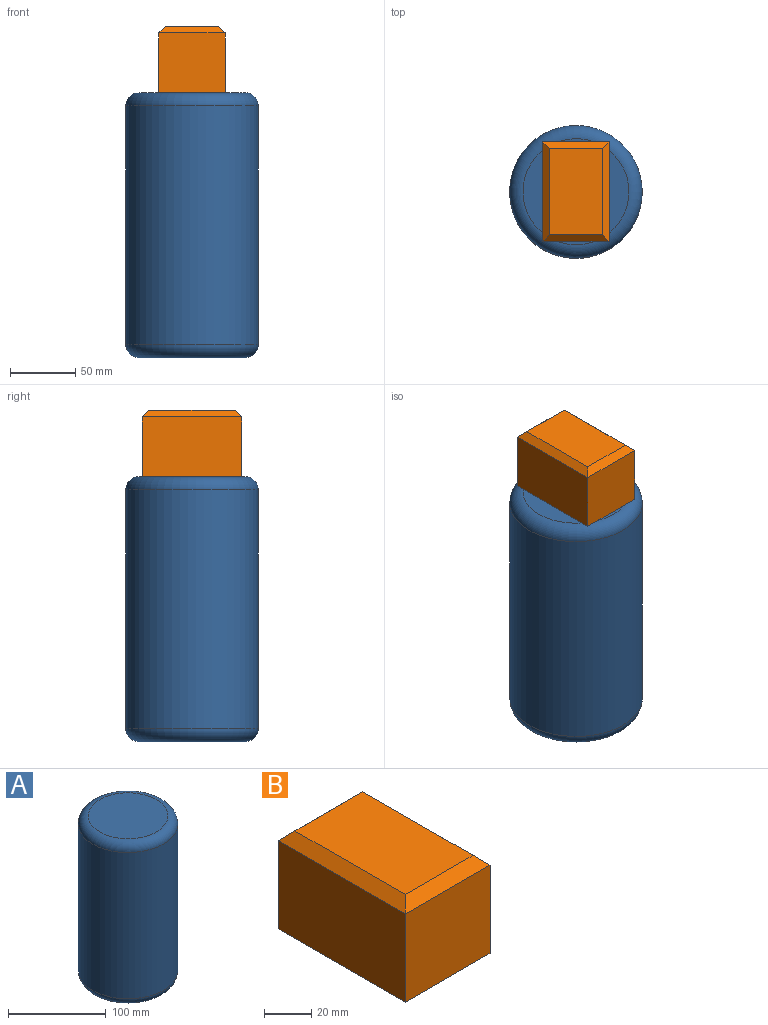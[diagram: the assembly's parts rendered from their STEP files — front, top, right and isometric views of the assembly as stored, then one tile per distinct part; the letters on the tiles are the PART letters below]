
ASSEMBLY  parts=2 mates=1
PART A: 5 faces, bbox 110x110x203.2 mm
  f0: cylinder r=50.8mm len=182.88mm, axis (0,0,-1), area 58372.7mm2, adj f3,f4
  f1: plane 81.28x81.28mm, normal (0,0,1), area 5188.7mm2, adj f4
  f2: plane 81.28x81.28mm, normal (0,0,-1), area 5188.7mm2, adj f3
  f3: torus R=40.64mm, axis (0,0,1), area 4723.8mm2, adj f0,f2
  f4: torus R=40.64mm, axis (0,0,1), area 4723.8mm2, adj f0,f1
PART B: 10 faces, bbox 50.8x76.2x50.8 mm
  f0: plane 76.2x45.72mm, normal (-1,0,0), area 3483.9mm2, adj f1,f3,f5,f9
  f1: plane 50.8x45.72mm, normal (0,-1,0), area 2322.6mm2, adj f0,f2,f5,f8
  f2: plane 76.2x45.72mm, normal (1,0,0), area 3483.9mm2, adj f1,f3,f5,f6
  f3: plane 50.8x45.72mm, normal (0,1,0), area 2322.6mm2, adj f0,f2,f5,f7
  f4: plane 66.04x40.64mm, normal (0,0,1), area 2683.9mm2, adj f6,f7,f8,f9
  f5: plane 76.2x50.8mm, normal (0,0,-1), area 3871mm2, adj f0,f1,f2,f3
  f6: plane 76.2x5.08mm, normal (0.71,0,0.71), area 510.9mm2, adj f2,f4,f7,f8
  f7: plane 50.8x5.08mm, normal (0,0.71,0.71), area 328.5mm2, adj f3,f4,f6,f9
  f8: plane 50.8x5.08mm, normal (0,-0.71,0.71), area 328.5mm2, adj f1,f4,f6,f9
  f9: plane 76.2x5.08mm, normal (-0.71,0,0.71), area 510.9mm2, adj f0,f4,f7,f8
PLACE A t=(-51.27,19.38,-28.12)mm
PLACE B t=(-50.78,16.9,175.08)mm
MATE planar B.f5 <-> A.f0  axis (0,0,-1) through (-51.27,19.38,175.08)mm
